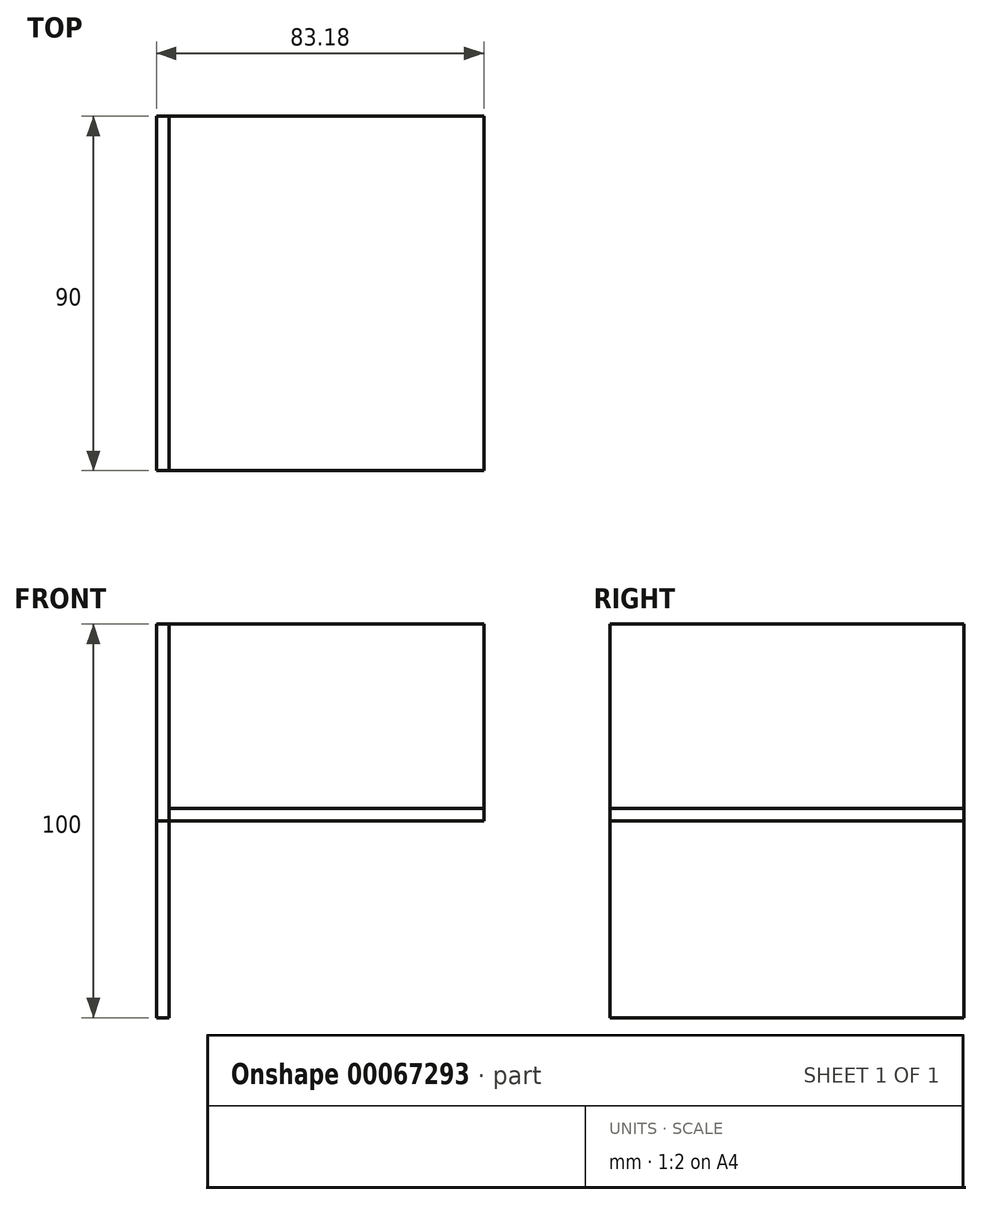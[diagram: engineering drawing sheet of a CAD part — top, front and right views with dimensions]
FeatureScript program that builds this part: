
annotation { "Feature Type Name" : "Feature", "Feature Type Description" : "" }
export const myFeature = defineFeature(function(context is Context, id is Id, definition is map)
    precondition{}
    {
        {
            var Q0;
            Q0=qCreatedBy(makeId("Front.planeOp"),FACE);
            var sketch = newSketch(context, id + "F0", { "sketchPlane" : qUnion([Q0])});
            skLineSegment(sketch, "E0.rect.bottom", {"start": v(-41.59, -25) * mm, "end": v(41.59, -25) * mm});
            skLineSegment(sketch, "E0.rect.top", {"start": v(-41.59, 25) * mm, "end": v(41.59, 25) * mm});
            skLineSegment(sketch, "E0.rect.left", {"start": v(-41.59, -25) * mm, "end": v(-41.59, 25) * mm});
            skLineSegment(sketch, "E0.rect.right", {"start": v(41.59, -25) * mm, "end": v(41.59, 25) * mm});
            skPoint(sketch, "E0.rect.middle", {"position": v(0, 0) * mm});
            skSolve(sketch);
        }
        {
            var Q0;
            Q0=makeQuery(id+"F0.imprint","IMPRINT",FACE,{"disambiguationData":[TD([[makeQuery(id+"F0.imprint","IMPRINT",EDGE,{"derivedFrom":sQuery(id+"F0.wireOp",EDGE,"E0.rect.bottom")}),1.0]])]});
            var Q1;
            Q1 = qSketchRegion(id + "F2", true);
            extrude(context, id + "F1", {"entities" : qUnion([Q0, Q1]), "oppositeDirection" : true, "depth" : 1 / 203.2 * mm});
        }
        {
            var Q0;
            Q0=qCreatedBy(makeId("Front.planeOp"),FACE);
            var sketch = newSketch(context, id + "F2", { "sketchPlane" : qUnion([Q0])});
            skLineSegment(sketch, "E1.bottom", {"start": v(-38.41, 25) * mm, "end": v(-41.59, 25) * mm});
            skLineSegment(sketch, "E1.top", {"start": v(-38.41, -25) * mm, "end": v(-41.59, -25) * mm});
            skLineSegment(sketch, "E1.left", {"start": v(-38.41, 25) * mm, "end": v(-38.41, -25) * mm});
            skLineSegment(sketch, "E1.right", {"start": v(-41.59, 25) * mm, "end": v(-41.59, -25) * mm});
            skSolve(sketch);
        }
        {
            var Q0;
            Q0 = qSketchRegion(id + "F2", true);
            extrude(context, id + "F3", {"entities" : qUnion([Q0]), "depth" : 90 * mm});
        }
        {
            var Q0;
            Q0=qCreatedBy(makeId("Front.planeOp"),FACE);
            var sketch = newSketch(context, id + "F4", { "sketchPlane" : qUnion([Q0])});
            skLineSegment(sketch, "E2.bottom", {"start": v(41.59, 25) * mm, "end": v(38.41, 25) * mm});
            skLineSegment(sketch, "E2.top", {"start": v(41.59, -25) * mm, "end": v(38.41, -25) * mm});
            skLineSegment(sketch, "E2.left", {"start": v(41.59, 25) * mm, "end": v(41.59, -25) * mm});
            skLineSegment(sketch, "E2.right", {"start": v(38.41, 25) * mm, "end": v(38.41, -25) * mm});
            skSolve(sketch);
        }
        {
            var Q0;
            Q0 = qSketchRegion(id + "F4", true);
            extrude(context, id + "F5", {"entities" : qUnion([Q0]), "depth" : 80 * mm});
        }
        {
            var Q0;
            Q0=qCreatedBy(makeId("Front.planeOp"),FACE);
            var sketch = newSketch(context, id + "F6", { "sketchPlane" : qUnion([Q0])});
            skLineSegment(sketch, "E3.bottom", {"start": v(-38.41, -21.82) * mm, "end": v(41.59, -21.82) * mm});
            skLineSegment(sketch, "E3.top", {"start": v(-38.41, -25) * mm, "end": v(41.59, -25) * mm});
            skLineSegment(sketch, "E3.left", {"start": v(-38.41, -21.82) * mm, "end": v(-38.41, -25) * mm});
            skLineSegment(sketch, "E3.right", {"start": v(41.59, -21.82) * mm, "end": v(41.59, -25) * mm});
            skSolve(sketch);
        }
        {
            var Q0;
            Q0 = qSketchRegion(id + "F6", true);
            extrude(context, id + "F7", {"entities" : qUnion([Q0]), "depth" : 90 * mm});
        }
        {
            var Q0;
            Q0=qCreatedBy(makeId("Front.planeOp"),FACE);
            var sketch = newSketch(context, id + "F8", { "sketchPlane" : qUnion([Q0])});
            skLineSegment(sketch, "E4.bottom", {"start": v(-38.41, 25) * mm, "end": v(41.59, 25) * mm});
            skLineSegment(sketch, "E4.top", {"start": v(-38.41, 21.82) * mm, "end": v(41.59, 21.82) * mm});
            skLineSegment(sketch, "E4.left", {"start": v(-38.41, 25) * mm, "end": v(-38.41, 21.82) * mm});
            skLineSegment(sketch, "E4.right", {"start": v(41.59, 25) * mm, "end": v(41.59, 21.82) * mm});
            skSolve(sketch);
        }
        {
            var Q0;
            Q0 = qSketchRegion(id + "F8", true);
            extrude(context, id + "F9", {"entities" : qUnion([Q0]), "depth" : 80 * mm});
        }
        {
            var Q0;
            Q0=qCreatedBy(makeId("Front.planeOp"),FACE);
            var sketch = newSketch(context, id + "F10", { "sketchPlane" : qUnion([Q0])});
            skLineSegment(sketch, "E5.bottom", {"start": v(-41.59, -25) * mm, "end": v(-38.41, -25) * mm});
            skLineSegment(sketch, "E5.top", {"start": v(-41.59, -75) * mm, "end": v(-38.41, -75) * mm});
            skLineSegment(sketch, "E5.left", {"start": v(-41.59, -25) * mm, "end": v(-41.59, -75) * mm});
            skLineSegment(sketch, "E5.right", {"start": v(-38.41, -25) * mm, "end": v(-38.41, -75) * mm});
            skSolve(sketch);
        }
        {
            var Q0;
            Q0 = qSketchRegion(id + "F10", true);
            extrude(context, id + "F11", {"entities" : qUnion([Q0]), "depth" : 90 * mm, "hasSecondDirection" : true, "secondDirectionOppositeDirection" : true, "secondDirectionDepth" : 1 / 203.2 * mm});
        }
        {
            var Q0;
            Q0=makeQuery(id+"F5.opExtrude","SWEPT_FACE",FACE,{"disambiguationData":[OSD([sQuery(id+"F4.wireOp",EDGE,"E2.left")])]});
            var sketch = newSketch(context, id + "F12", { "sketchPlane" : qUnion([Q0])});
            skCircle(sketch, "E6", {"center": v(-40, -15) * mm, "radius": 2.5 * mm});
            skPoint(sketch, "E6.centerSnap0", {"position": v(-40, -25) * mm});
            skSolve(sketch);
        }
        {
            var Q0;
            Q0 = qSketchRegion(id + "F12", true);
            var Q1;
            Q1=makeQuery(id+"F5.opExtrude","SWEPT_BODY",BODY,{"disambiguationData":[OSD([sQuery(id+"F4.wireOp",EDGE,"E2.bottom"),sQuery(id+"F4.wireOp",EDGE,"E2.top"),sQuery(id+"F4.wireOp",EDGE,"E2.left"),sQuery(id+"F4.wireOp",EDGE,"E2.right")])]});
            extrude(context, id + "F13", {"entities" : qUnion([Q0]), "operationType" : NewBodyOperationType.REMOVE, "endBound" : BoundingType.UP_TO_BODY, "oppositeDirection" : true, "endBoundEntityBody" : qUnion([Q1]), "depth" : 25 * mm});
        }
        {
            var Q0;
            Q0=makeQuery(id+"F5.opExtrude","SWEPT_BODY",BODY,{"disambiguationData":[OSD([sQuery(id+"F4.wireOp",EDGE,"E2.bottom"),sQuery(id+"F4.wireOp",EDGE,"E2.top"),sQuery(id+"F4.wireOp",EDGE,"E2.left"),sQuery(id+"F4.wireOp",EDGE,"E2.right")])]});
            deleteBodies(context, id + "F14", {"entities" : qUnion([Q0])});
        }
        {
            var Q0;
            Q0=makeQuery(id+"F9.opExtrude","SWEPT_BODY",BODY,{"disambiguationData":[OSD([sQuery(id+"F8.wireOp",EDGE,"E4.bottom"),sQuery(id+"F8.wireOp",EDGE,"E4.top"),sQuery(id+"F8.wireOp",EDGE,"E4.left"),sQuery(id+"F8.wireOp",EDGE,"E4.right")])]});
            deleteBodies(context, id + "F15", {"entities" : qUnion([Q0])});
        }
    });
